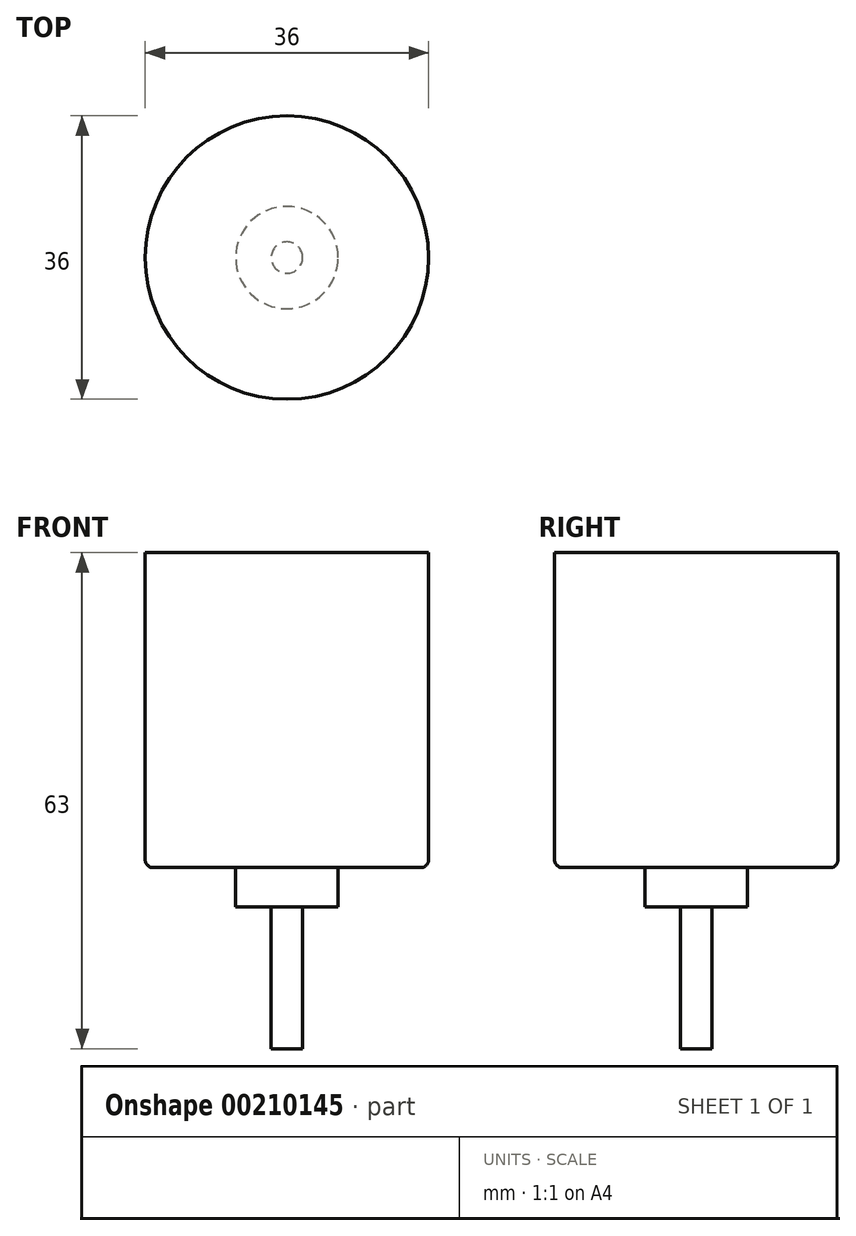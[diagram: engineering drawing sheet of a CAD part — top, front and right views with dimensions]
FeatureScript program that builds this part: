
annotation { "Feature Type Name" : "Feature", "Feature Type Description" : "" }
export const myFeature = defineFeature(function(context is Context, id is Id, definition is map)
    precondition{}
    {
        {
            var Q0;
            Q0=qCreatedBy(makeId("Top.planeOp"),FACE);
            var sketch = newSketch(context, id + "F0", { "sketchPlane" : qUnion([Q0])});
            skCircle(sketch, "E0", {"center": v(0, 0) * mm, "radius": 18 * mm});
            skSolve(sketch);
        }
        {
            var Q0;
            Q0=makeQuery(id+"F0.imprint","IMPRINT",FACE,{"disambiguationData":[TD([[makeQuery(id+"F0.imprint","IMPRINT",EDGE,{"derivedFrom":sQuery(id+"F0.wireOp",EDGE,"E0")}),1.0]])]});
            extrude(context, id + "F1", {"entities" : qUnion([Q0]), "depth" : 40 * mm});
        }
        {
            var Q0;
            Q0=qCreatedBy(makeId("Top.planeOp"),FACE);
            var sketch = newSketch(context, id + "F2", { "sketchPlane" : qUnion([Q0])});
            skCircle(sketch, "E1", {"center": v(0, 0) * mm, "radius": 6.5 * mm});
            skSolve(sketch);
        }
        {
            var Q0;
            Q0=makeQuery(id+"F2.imprint","IMPRINT",FACE,{"disambiguationData":[TD([[makeQuery(id+"F2.imprint","IMPRINT",EDGE,{"derivedFrom":sQuery(id+"F2.wireOp",EDGE,"E1")}),1.0]])]});
            extrude(context, id + "F3", {"entities" : qUnion([Q0]), "operationType" : NewBodyOperationType.ADD, "oppositeDirection" : true, "depth" : 5 * mm});
        }
        {
            var Q0;
            Q0=qCreatedBy(makeId("Top.planeOp"),FACE);
            var sketch = newSketch(context, id + "F4", { "sketchPlane" : qUnion([Q0])});
            skCircle(sketch, "E2", {"center": v(0, 0) * mm, "radius": 2 * mm});
            skSolve(sketch);
        }
        {
            var Q0;
            Q0=qSketchRegion(id+"F4",true);
            extrude(context, id + "F5", {"entities" : qUnion([Q0]), "operationType" : NewBodyOperationType.ADD, "oppositeDirection" : true, "depth" : 23 * mm});
        }
        {
            var Q0;
            Q0=makeQuery(id+"F1.opExtrude","CAP_EDGE",EDGE,{"disambiguationData":[OSD([sQuery(id+"F0.wireOp",EDGE,"E0")])],"isStart":true});
            fillet(context, id + "F6", {"entities" : qUnion([Q0]), "radius" : 1 * mm, "tangentPropagation" : true, "allowEdgeOverflow" : false});
        }
    });
